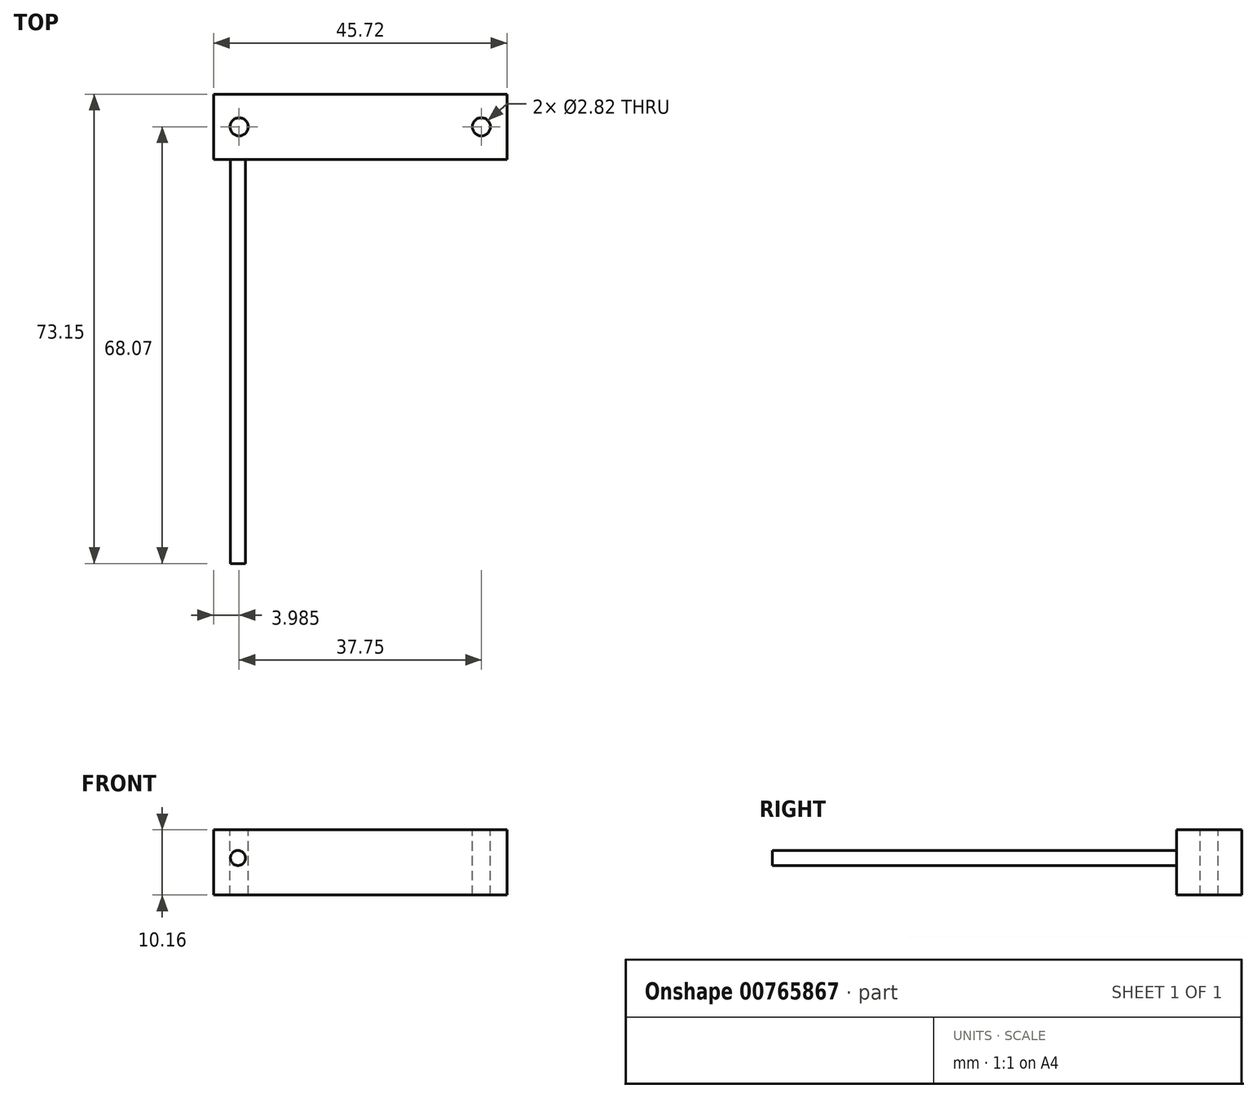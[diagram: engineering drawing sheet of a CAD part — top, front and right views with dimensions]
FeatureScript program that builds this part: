
annotation { "Feature Type Name" : "Feature", "Feature Type Description" : "" }
export const myFeature = defineFeature(function(context is Context, id is Id, definition is map)
    precondition{}
    {
        {
            var Q0;
            Q0=qCreatedBy(makeId("Top.planeOp"),FACE);
            var sketch = newSketch(context, id + "F0", { "sketchPlane" : qUnion([Q0])});
            skLineSegment(sketch, "E0.bottom", {"start": v(-22.86, 5.08) * mm, "end": v(22.86, 5.08) * mm});
            skLineSegment(sketch, "E0.top", {"start": v(-22.86, -5.08) * mm, "end": v(22.86, -5.08) * mm});
            skLineSegment(sketch, "E0.left", {"start": v(-22.86, 5.08) * mm, "end": v(-22.86, -5.08) * mm});
            skLineSegment(sketch, "E0.right", {"start": v(22.86, 5.08) * mm, "end": v(22.86, -5.08) * mm});
            skPoint(sketch, "E0.middle", {"position": v(0, 0) * mm});
            skSolve(sketch);
        }
        {
            var Q0;
            Q0=makeQuery(id+"F0.imprint","IMPRINT",FACE,{"disambiguationData":[TD([[makeQuery(id+"F0.imprint","IMPRINT",EDGE,{"derivedFrom":sQuery(id+"F0.wireOp",EDGE,"E0.bottom")}),-1.0]])]});
            extrude(context, id + "F1", {"entities" : qUnion([Q0]), "depth" : 10.16 * mm, "offsetDistance" : 25.4 * mm});
        }
        {
            var Q0;
            Q0=makeQuery(id+"F1.opExtrude","CAP_FACE",FACE,{"disambiguationData":[OSD([sQuery(id+"F0.wireOp",EDGE,"E0.bottom"),sQuery(id+"F0.wireOp",EDGE,"E0.top"),sQuery(id+"F0.wireOp",EDGE,"E0.left"),sQuery(id+"F0.wireOp",EDGE,"E0.right")])],"isStart":false});
            var sketch = newSketch(context, id + "F2", { "sketchPlane" : qUnion([Q0])});
            skCircle(sketch, "E1", {"center": v(-18.87, 0) * mm, "radius": 1.4 * mm});
            skCircle(sketch, "E2.MirrorC", {"center": v(18.87, 0) * mm, "radius": 1.4 * mm});
            skSolve(sketch);
        }
        {
            var Q0;
            Q0 = qSketchRegion(id + "F2", true);
            extrude(context, id + "F3", {"entities" : qUnion([Q0]), "operationType" : NewBodyOperationType.REMOVE, "oppositeDirection" : true, "depth" : 25.4 * mm, "offsetDistance" : 25.4 * mm});
        }
        {
            var Q0;
            Q0=makeQuery(id+"F1.opExtrude","SWEPT_FACE",FACE,{"disambiguationData":[OSD([sQuery(id+"F0.wireOp",EDGE,"E0.top")])]});
            var sketch = newSketch(context, id + "F4", { "sketchPlane" : qUnion([Q0])});
            skCircle(sketch, "E3", {"center": v(-19.05, 5.78) * mm, "radius": 1.17 * mm});
            skSolve(sketch);
        }
        {
            var Q0;
            Q0=makeQuery(id+"F4.imprint","IMPRINT",FACE,{"disambiguationData":[TD([[makeQuery(id+"F4.imprint","IMPRINT",EDGE,{"derivedFrom":sQuery(id+"F4.wireOp",EDGE,"E3")}),1.0]])]});
            extrude(context, id + "F5", {"entities" : qUnion([Q0]), "operationType" : NewBodyOperationType.ADD, "depth" : 63 * mm, "offsetDistance" : 25.4 * mm});
        }
    });
